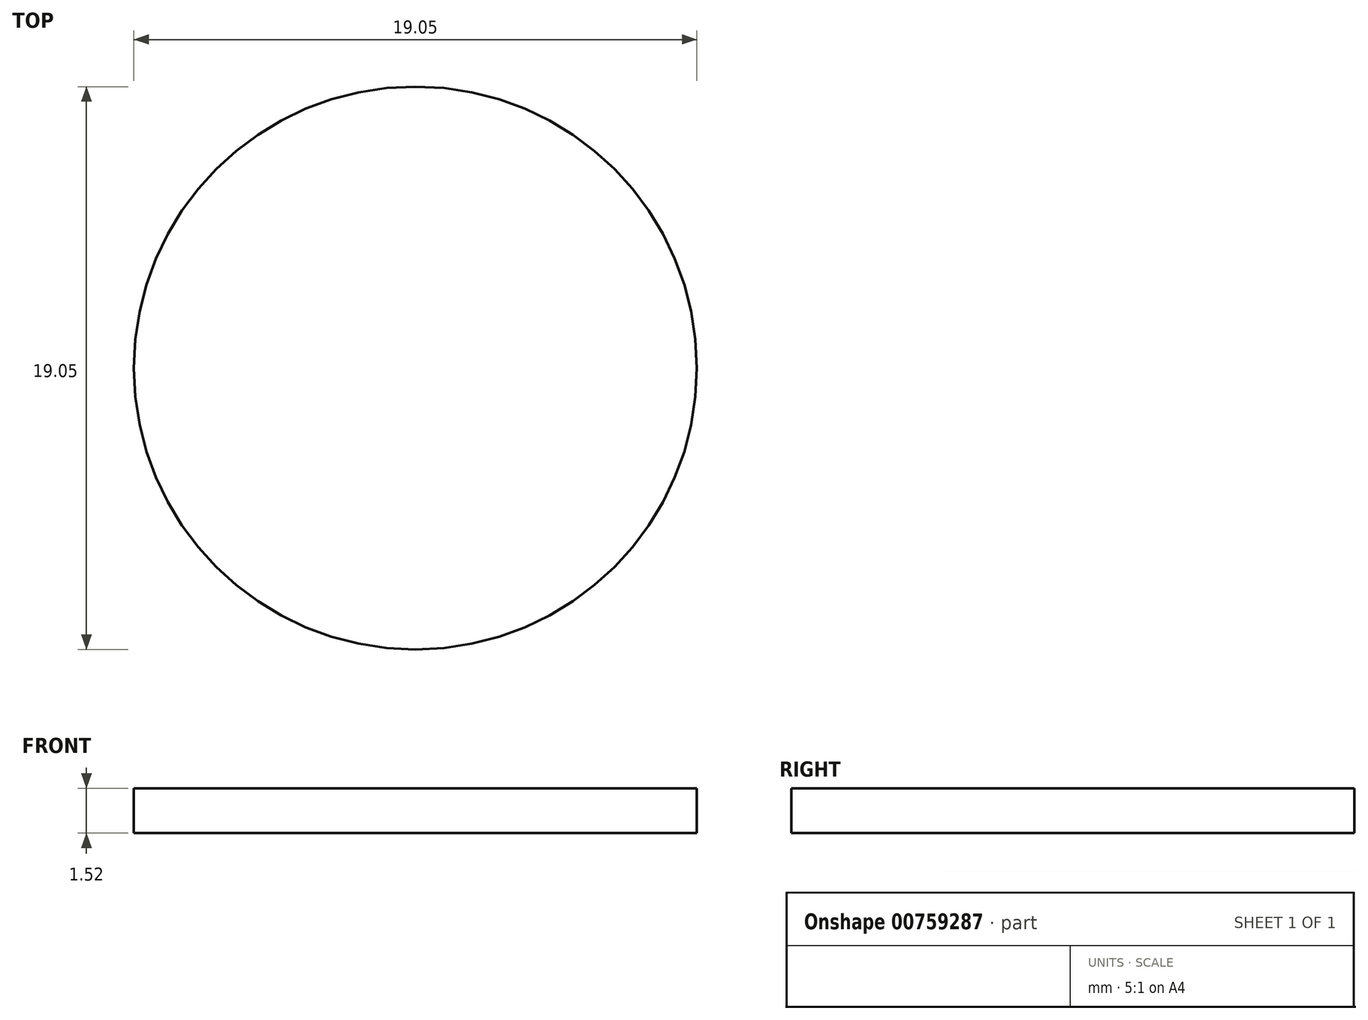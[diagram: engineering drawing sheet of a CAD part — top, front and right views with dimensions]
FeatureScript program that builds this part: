
annotation { "Feature Type Name" : "Feature", "Feature Type Description" : "" }
export const myFeature = defineFeature(function(context is Context, id is Id, definition is map)
    precondition{}
    {
        {
            var Q0;
            Q0=qCreatedBy(makeId("Top.planeOp"),FACE);
            var sketch = newSketch(context, id + "F0", { "sketchPlane" : qUnion([Q0])});
            skCircle(sketch, "E0", {"center": v(-99.55, 10.1) * mm, "radius": 9.52 * mm});
            skSolve(sketch);
        }
        {
            var Q0;
            Q0=makeQuery(id+"F0.imprint","IMPRINT",FACE,{"disambiguationData":[TD([[makeQuery(id+"F0.imprint","IMPRINT",EDGE,{"derivedFrom":sQuery(id+"F0.wireOp",EDGE,"E0")}),1.0]])]});
            extrude(context, id + "F1", {"entities" : qUnion([Q0]), "depth" : 1.52 * mm, "offsetDistance" : 25.4 * mm});
        }
    });
